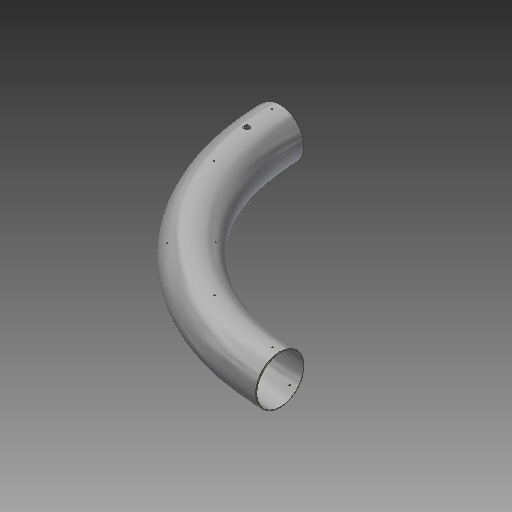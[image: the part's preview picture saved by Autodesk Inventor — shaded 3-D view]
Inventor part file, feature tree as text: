
AUTODESK INVENTOR PART (.ipt)
format: ipt  version: 2017.3 (Build 213257000, 257)  size: 357,376 bytes
history: native  units: in
note: dims shown in document units (in); Inventor stores cm internally (conversion verified against a paired STEP export)
features: plane x9, pattern_circular x6, other x5, hole x3, chamfer x2, sketch x2, revolve x1, split x1, extrude x1
ambient origin geometry x8: Origin, YZ Plane, XZ Plane, XY Plane, X Axis, Y Axis, Z Axis, Center Point
bodies: Solid1 (feature_tree)
feature tree (30):
  revolve  "Revolution1"  [1 undecoded]
  chamfer  "Chamfer3"  Angle=90.0deg  [1 undecoded]
  chamfer  "Chamfer4"  Distance=0.4375in
  plane  "Work Plane1"
  sketch  "Sketch4"  dims[d2=160.0in d3=90.0deg d14=0.4375in d15=0.125in d16=0.2577in d17=0.4375in d18=0.125in d19=0.2577in d20=18.01in d21=160.0in d22=27.2835in d23=4.125in d24=160.0in d25=6.0in d26=0.0148in d27=22.5deg d28=2.5625in d29=0.75in d30=0.375in d31=0.25in d32=0.5635in d33=1.0in d34=0.8108in d35=1.0in d36=0.0in d37=0.891in d38=0.553in d39=0.0246in d40=0.897in d41=0.375in d42=0.25in d43=0.5635in d44=0.91in d45=0.8108in d46=0.891in d47=0.553in d48=0.0246in d49=0.897in d50=0.375in d51=0.25in d52=0.5635in d53=0.91in d54=0.8108in d55=0.0148in d56=-160.0in d57=22.5deg d58=-160.0in d59=1.1811in d60=135.0deg d62=0.7874in d63=180.0deg d65=0.7874in d66=45.0deg d68=0.7874in d69=0.5889in d71=0.0675in d72=0.0675in d73=-160.0in d74=45.0deg d75=-160.0in d76=0.7874in d77=45.0deg d79=0.7874in d80=360.0deg]
  hole  "Hole1"  [1 undecoded]
  split  "Split1"
  other  "Work Axis3"
  hole  "Hole2"  [1 undecoded]
  hole  "Hole3"  [1 undecoded]
  plane  "Work Plane2"
  other  "Work Axis1"
  other  "Work Axis2"
  pattern_circular  "Circular Pattern1"  [2 undecoded]
  pattern_circular  "Circular Pattern2"  [2 undecoded]
  pattern_circular  "Circular Pattern3"  [2 undecoded]
  pattern_circular  "Circular Pattern4"  [2 undecoded]
  other  "Work Axis4"
  pattern_circular  "Circular Pattern5"  [2 undecoded]
  pattern_circular  "Circular Pattern6"  [2 undecoded]
  sketch  "Sketch1"  dims[d0=36.0in d1=35.0in]
  other  "Srf1"
  plane  "Work Plane3"
  plane  "Work Plane4"
  plane  "Work Plane5"
  plane  "Work Plane6"
  plane  "Work Plane7"
  plane  "Work Plane8"
  plane  "Work Plane9"
  extrude  "ExtrusionSrf1"  Depth=0.0148in
note: 17 required parameter values undecoded (feature->parameter linkage not recoverable at this tier; creation-order binding heuristic only, values carry confidence <= 0.55)